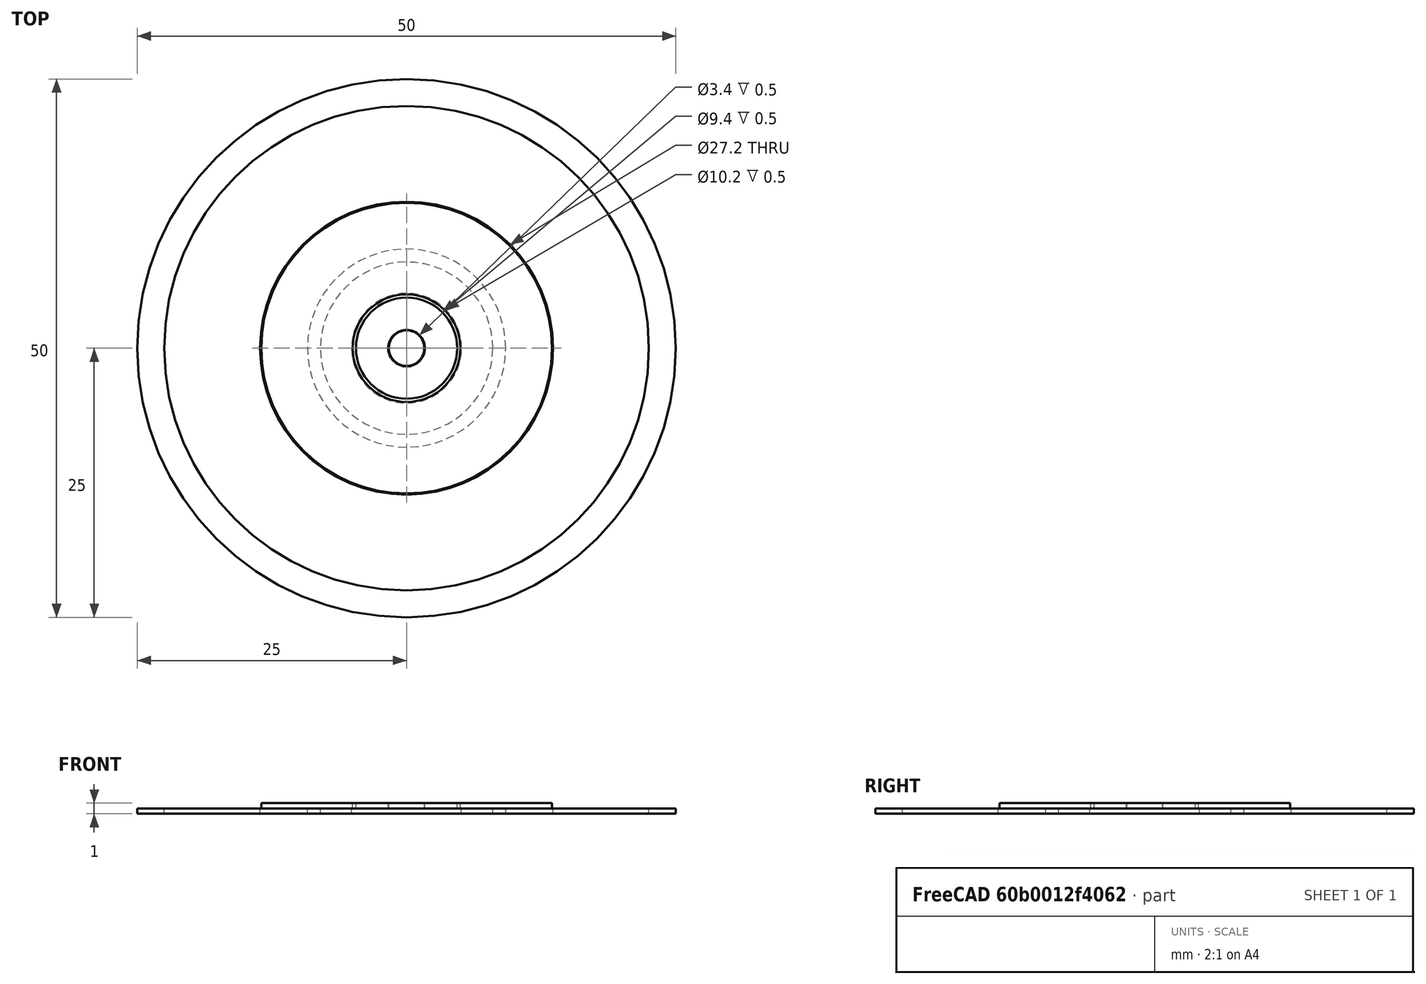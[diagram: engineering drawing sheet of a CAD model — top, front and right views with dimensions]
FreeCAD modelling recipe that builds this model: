
FCSTD DOCUMENT  (FreeCAD 0.18.3R)
Label: RFC Roundels
License: All rights reserved
LicenseURL: http://en.wikipedia.org/wiki/All_rights_reserved
objects: Part::Cylinder×12, Part::Cut×4, Part::FeaturePython×2
note: 18 computed .brp shape members not serialized (recipe doc carries the construction recipe); baked Part::Feature solids carry a one-line shape summary decoded from their .brp

FEATURE [Part::Cylinder] Cylinder006
  Angle = 360
  AttacherType = Attacher::AttachEngine3D
  Height = 0.5
  Radius = 8
FEATURE [Part::Cylinder] Cylinder007
  Angle = 360
  AttacherType = Attacher::AttachEngine3D
  Height = 1
  Radius = 5
FEATURE [Part::Cylinder] Cylinder008
  Angle = 360
  AttacherType = Attacher::AttachEngine3D
  Height = 0.5
  Placement = pos=(0,0,0.5) rot=(0,0,1;0rad)
  Radius = 1.7
FEATURE [Part::Cylinder] Cylinder009
  Angle = 360
  AttacherType = Attacher::AttachEngine3D
  Height = 0.5
  Radius = 9.2
FEATURE [Part::Cylinder] Cylinder010  label="Small Red"
  Angle = 360
  AttacherType = Attacher::AttachEngine3D
  Height = 0.5
  Placement = pos=(0,0,0.5) rot=(0,0,1;0rad)
  Radius = 1.65
FEATURE [Part::Cut] Cut
  Base = -> Cylinder007
  Tool = -> Cylinder008
FEATURE [Part::Cylinder] Cylinder011
  Angle = 360
  AttacherType = Attacher::AttachEngine3D
  Height = 10
  Radius = 5.1
FEATURE [Part::Cut] Cut003  label="Small Blue"
  Base = -> Cylinder006
  Tool = -> Cylinder011
FEATURE [Part::FeaturePython] Embed  label="Small White"  # WARN: FeaturePython — macro-defined, semantics opaque (R4)
  Base = -> Cylinder009
  Tolerance = 0
  Tool = -> Cut
FEATURE [Part::Cylinder] Cylinder012  label="Large Red"
  Angle = 360
  AttacherType = Attacher::AttachEngine3D
  Height = 0.5
  Placement = pos=(0,0,0.5) rot=(0,0,1;0rad)
  Radius = 4.7
FEATURE [Part::Cylinder] Cylinder015
  Angle = 360
  AttacherType = Attacher::AttachEngine3D
  Height = 0.5
  Radius = 25
FEATURE [Part::Cylinder] Cylinder016
  Angle = 360
  AttacherType = Attacher::AttachEngine3D
  Height = 0.5
  Radius = 13.5
FEATURE [Part::Cylinder] Cylinder017  label="Red001"
  Angle = 360
  AttacherType = Attacher::AttachEngine3D
  Height = 0.5
  Radius = 4.7
FEATURE [Part::Cut] Cut004
  Base = -> Cylinder016
  Placement = pos=(0,0,0.5) rot=(0,0,1;0rad)
  Tool = -> Cylinder017
FEATURE [Part::FeaturePython] Embed001  label="Large White"  # WARN: FeaturePython — macro-defined, semantics opaque (R4)
  Base = -> Cylinder015
  Tolerance = 0
  Tool = -> Cut004
FEATURE [Part::Cylinder] Cylinder018
  Angle = 360
  AttacherType = Attacher::AttachEngine3D
  Height = 0.5
  Radius = 13.6
FEATURE [Part::Cylinder] Cylinder019
  Angle = 360
  AttacherType = Attacher::AttachEngine3D
  Height = 0.5
  Radius = 22.5
FEATURE [Part::Cut] Cut007  label="Large Blue"
  Base = -> Cylinder019
  Tool = -> Cylinder018
